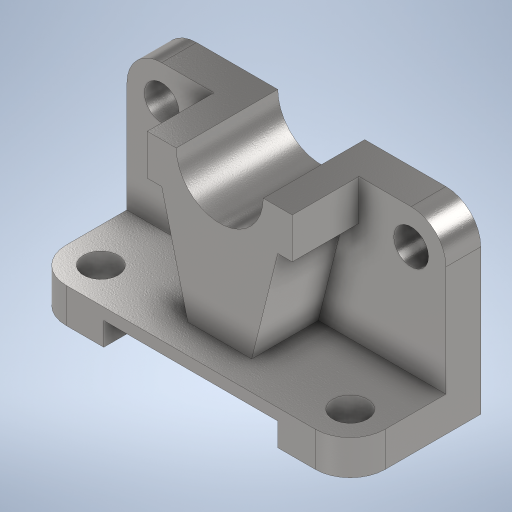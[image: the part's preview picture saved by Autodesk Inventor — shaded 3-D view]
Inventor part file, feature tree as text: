
AUTODESK INVENTOR PART (.ipt)
format: ipt  version: 2024 (Build 280153000, 153)  size: 408,576 bytes
history: native  units: mm
features: sketch x11, extrude x5, hole x4, fillet x1, plane x1, loft x1
ambient origin geometry x8: Origin, YZ Plane, XZ Plane, XY Plane, X Axis, Y Axis, Z Axis, Center Point
bodies: Volumenkörper1 (feature_tree)
feature tree (23):
  extrude  "Extrusion1"  Depth=45.0mm
  extrude  "Extrusion2"  Depth=12.0mm
  fillet  "Rundung1"  Radius=62.0mm
  plane  "Arbeitsebene1"
  extrude  "Extrusion4"  Depth=12.0mm
  loft  "Erhebung3"
  extrude  "Extrusion5"  Depth=50.0mm
  hole  "Bohrung1"  [1 undecoded]
  hole  "Bohrung2"  [1 undecoded]
  hole  "Bohrung3"  [1 undecoded]
  hole  "Bohrung4"  [1 undecoded]
  extrude  "Extrusion6"  Depth=60.0mm
  sketch  "Skizze1"  dims[d0=110.0mm d1=45.0mm]
  sketch  "Skizze2"  dims[d2=12.0mm d3=0.0mm d4=12.0mm d5=62.0mm]
  sketch  "Skizze3"  dims[d6=12.0mm d7=0.0mm d8=12.0mm]
  sketch  "Skizze5"  dims[d9=22.0mm d10=23.0mm]
  sketch  "Skizze9"  dims[d11=48.0mm d12=50.0mm]
  sketch  "Skizze10"  dims[d13=35.0mm d22=12.0mm d23=0.0mm]
  sketch  "Skizze11"  dims[d30=40.0mm d31=23.0mm]
  sketch  "Skizze12"  dims[d32=0.0mm d33=90.0deg d34=0.0mm d35=90.0deg]
  sketch  "Skizze13"  dims[d38=30.0mm d39=10.0mm]
  sketch  "Skizze14"  dims[d40=10.0mm d41=0.0mm]
  sketch  "Skizze15"  dims[d42=12.0mm d43=6.0mm d44=4.0mm d45=2.0mm d46=90.0deg d47=8.0mm d48=0.0mm d49=12.0mm d50=6.0mm d51=4.0mm d52=2.0mm d53=90.0deg d54=8.0mm d55=0.0mm d56=12.0mm d57=6.0mm d58=4.0mm d59=2.0mm d60=90.0deg d61=8.0mm d62=0.0mm d63=12.0mm d64=6.0mm d65=4.0mm d66=2.0mm d67=90.0deg d68=8.0mm d69=0.0mm d70=60.0mm d71=25.0mm d72=8.0mm d73=10.0mm d74=0.0mm]
note: 4 required parameter values undecoded (feature->parameter linkage not recoverable at this tier; creation-order binding heuristic only, values carry confidence <= 0.55)
